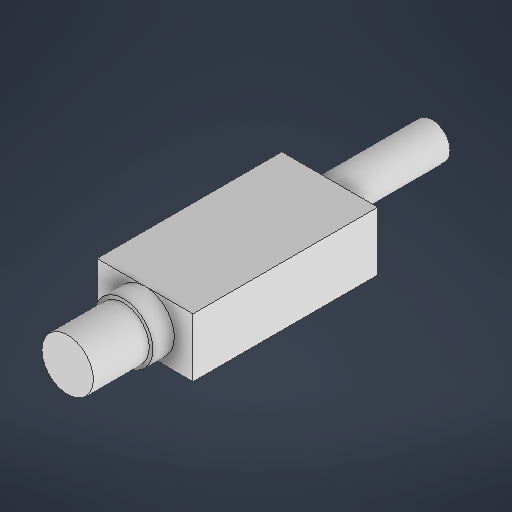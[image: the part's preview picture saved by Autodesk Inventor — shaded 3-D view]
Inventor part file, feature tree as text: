
AUTODESK INVENTOR PART (.ipt)
format: ipt  version: 2025 (Build 290162000, 162)  size: 257,536 bytes
history: native  units: in
note: dims shown in document units (in); Inventor stores cm internally (conversion verified against a paired STEP export)
features: extrude x4, sketch x4, hole x3
ambient origin geometry x8: Origin, YZ Plane, XZ Plane, XY Plane, X Axis, Y Axis, Z Axis, Center Point
bodies: Solid1 (feature_tree)
feature tree (11):
  extrude  "Extrusion1"  Depth=5.0787in
  sketch  "Sketch2"  dims[d2=1.6142in d3=0.0in d4=1.6142in]
  extrude  "Extrusion2"  Depth=1.6142in
  extrude  "Extrusion3"  Depth=2.126in TaperAngle=0.0deg
  extrude  "Extrusion5"  Depth=0.3937in
  sketch  "Sketch5"  dims[d8=0.5906in d9=0.0in d13=0.9843in d14=0.9843in d15=3.1496in d16=0.0in d17=0.1969in d19=0.1575in d20=0.1969in d23=2.6378in d24=3.1496in d25=4.3307in d28=0.1936in d29=0.3937in d30=0.1575in d31=0.0787in d32=90.0deg d33=0.3937in d34=0.0in d35=3.3465in d36=2.3622in d37=0.196in d38=0.3937in d39=0.1575in d40=0.0787in d41=90.0deg d42=0.3937in d43=0.0in d44=0.1575in d45=0.3937in d46=0.1575in d47=0.0787in d48=90.0deg d49=0.3937in d50=0.0in]
  hole  "Hole1"  [1 undecoded]
  hole  "Hole2"  [1 undecoded]
  hole  "Hole3"  [1 undecoded]
  sketch  "Sketch1"  dims[d0=2.6378in d1=5.0787in]
  sketch  "Sketch4"  dims[d5=1.4173in d6=2.126in d7=0.0in]
note: 3 required parameter values undecoded (feature->parameter linkage not recoverable at this tier; creation-order binding heuristic only, values carry confidence <= 0.55)
